# Revit family: QF_Vollrath_1554-C
name_source: partatom
category: Specialty Equipment
revit_build: Autodesk Revit 2016 (Build: 20151007_0715(x64)
units: mm (PartAtom-declared; Revit-internal decimal feet)

## family parameters
Always vertical = Yes
Cut with Voids When Loaded = No
OmniClass Number = 23.40.40.14.31
OmniClass Title = Cleaning and Disposal Equipment
Part Type = Normal
Room Calculation Point = No
Round Connector Dimension = Use Diameter
Shared = No
Work Plane-Based = Yes

## types (3) — shared parameters
Default Elevation = 4' - 0"
Depth = 1' - 3"
Description = Bar Sink
Indirect Waste Size = 2"
Manufacturer = Vollrath
Sink Basin Depth = 0' - 6 3/16"
Sink Depth = 0' - 10"
Sink Width = 0' - 11"
Width = 1' - 3"
zero-valued in all types: Weight in Pounds

## per-type parameters (varying)
| type | Model |
| 155-4 | 1554-C |
| 1554-C | 1554-C |
| K1554-C | K1554-C |

## geometry (parser evidence)
native form markers: Blend x39, Sweep x2
no freeform markers — native parametric forms only
